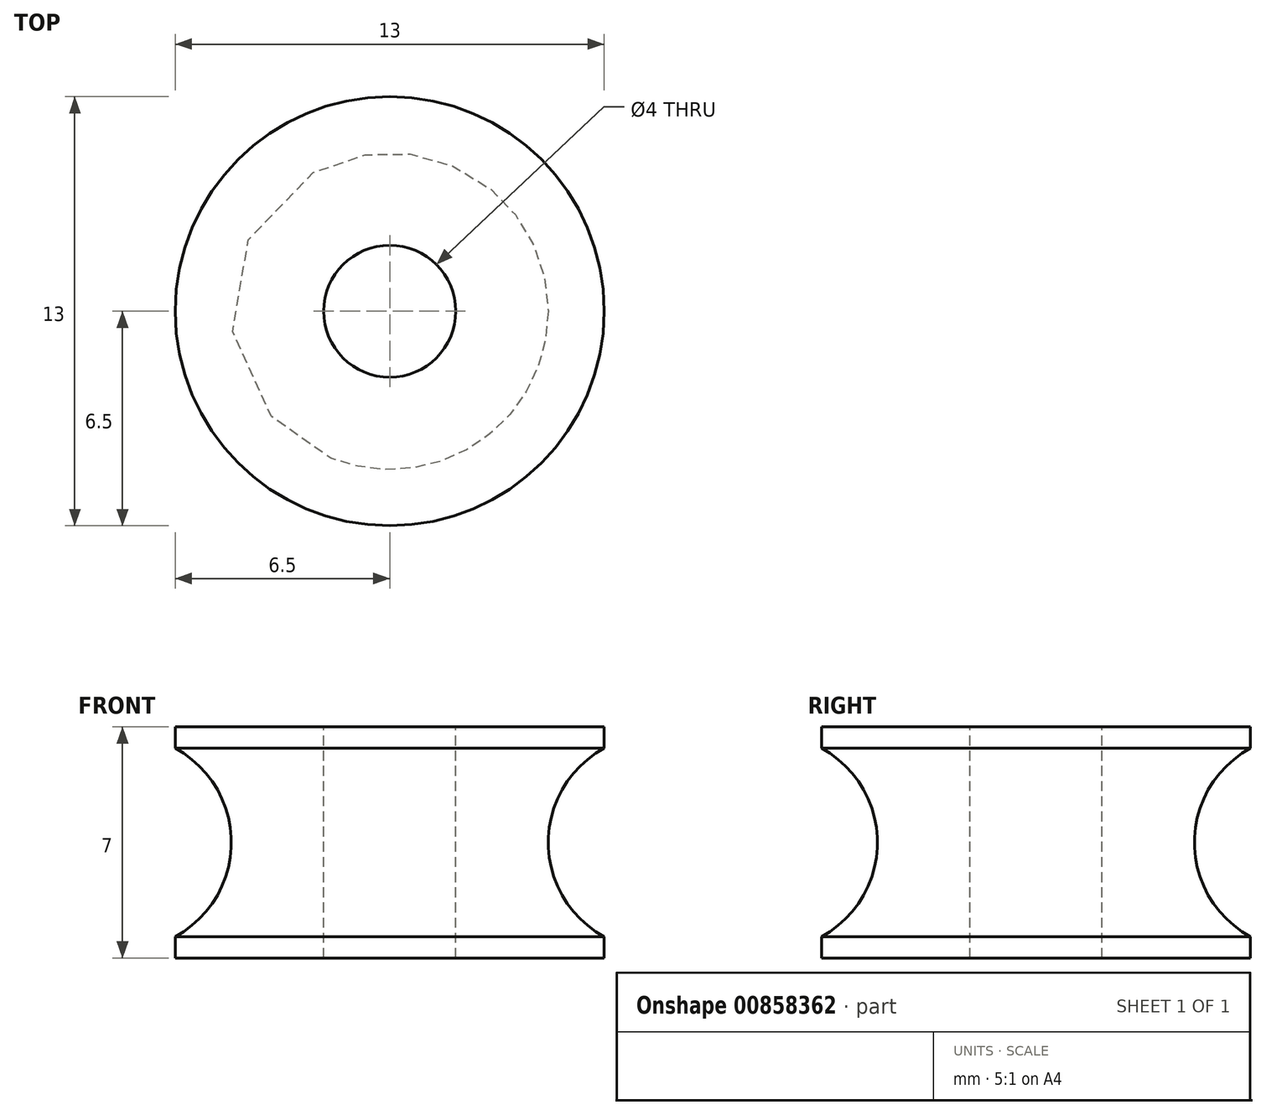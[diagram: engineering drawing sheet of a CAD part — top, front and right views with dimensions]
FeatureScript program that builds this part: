
annotation { "Feature Type Name" : "Feature", "Feature Type Description" : "" }
export const myFeature = defineFeature(function(context is Context, id is Id, definition is map)
    precondition{}
    {
        {
            var Q0;
            Q0=qCreatedBy(makeId("Front.planeOp"),FACE);
            var sketch = newSketch(context, id + "F0", { "sketchPlane" : qUnion([Q0])});
            skLineSegment(sketch, "E0", {"start": v(-2, -3.5) * mm, "end": v(-2, 3.5) * mm});
            skLineSegment(sketch, "E1", {"start": v(-2, 3.5) * mm, "end": v(-6.5, 3.5) * mm});
            skLineSegment(sketch, "E2", {"start": v(-6.5, 3.5) * mm, "end": v(-6.5, 2.86) * mm});
            skLineSegment(sketch, "E3", {"start": v(-6.5, -2.86) * mm, "end": v(-6.5, -3.5) * mm});
            skLineSegment(sketch, "E4", {"start": v(-6.5, -3.5) * mm, "end": v(-2, -3.5) * mm});
            skCircle(sketch, "E5", {"center": v(-8.05, 0) * mm, "radius": 3.25 * mm, "construction": true});
            skLineSegment(sketch, "E6", {"start": v(0, 0) * mm, "end": v(0, -16.78) * mm, "construction": true});
            skArc(sketch, "E7", {"start": v(-6.5, 2.86) * mm, "mid": v(-4.8, 0) * mm, "end": v(-6.5, -2.86) * mm});
            skSolve(sketch);
        }
        {
            var Q0;
            Q0=makeQuery(id+"F0.imprint","IMPRINT",FACE,{"disambiguationData":[TD([[makeQuery(id+"F0.imprint","IMPRINT",EDGE,{"derivedFrom":sQuery(id+"F0.wireOp",EDGE,"E0")}),1.0]])]});
            var Q1;
            Q1=sQuery(id+"F0.wireOp",EDGE,"E6");
            var Q2;
            Q2=sQuery(id+"F0.wireOp",EDGE,"E6");
            revolve(context, id + "F1", {"surfaceOperationType" : NewSurfaceOperationType.NEW, "entities" : qUnion([Q0]), "surfaceEntities" : qUnion([Q1]), "axis" : qUnion([Q2]), "revolveType" : RevolveType.FULL});
        }
    });
